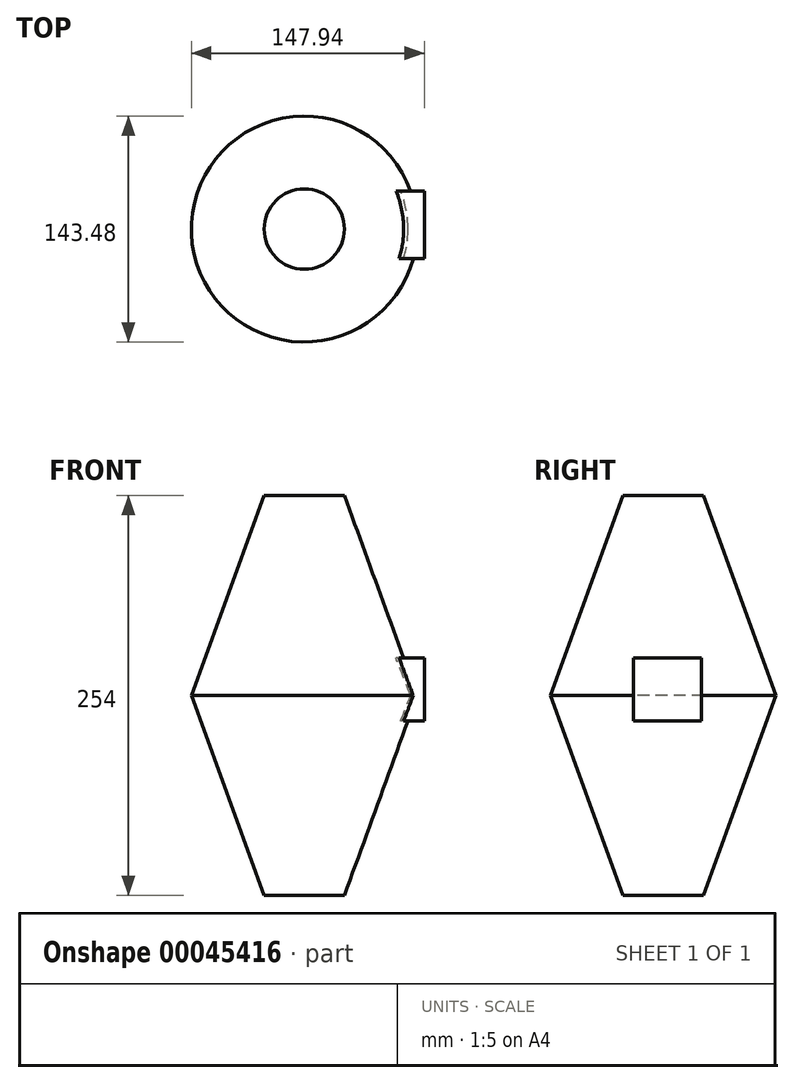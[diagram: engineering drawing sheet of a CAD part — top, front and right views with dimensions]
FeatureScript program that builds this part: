
annotation { "Feature Type Name" : "Feature", "Feature Type Description" : "" }
export const myFeature = defineFeature(function(context is Context, id is Id, definition is map)
    precondition{}
    {
        {
            var Q0;
            Q0=qCreatedBy(makeId("Top.planeOp"),FACE);
            var sketch = newSketch(context, id + "F0", { "sketchPlane" : qUnion([Q0])});
            skCircle(sketch, "E0", {"center": v(0, 0) * mm, "radius": 71.74 * mm});
            skSolve(sketch);
        }
        {
            var Q0;
            Q0 = qSketchRegion(id + "F0", true);
            extrude(context, id + "F1", {"entities" : qUnion([Q0]), "endBound" : BoundingType.SYMMETRIC, "depth" : 254 * mm, "hasDraft" : true, "draftAngle" : 20 * degree, "draftPullDirection" : true});
        }
        {
            var Q0;
            Q0=qCreatedBy(makeId("Right.planeOp"),FACE);
            var sketch = newSketch(context, id + "F2", { "sketchPlane" : qUnion([Q0])});
            skLineSegment(sketch, "E1.bottom", {"start": v(-18.76, -16.13) * mm, "end": v(24.17, -16.13) * mm});
            skLineSegment(sketch, "E1.top", {"start": v(-18.76, 23.72) * mm, "end": v(24.17, 23.72) * mm});
            skLineSegment(sketch, "E1.left", {"start": v(-18.76, -16.13) * mm, "end": v(-18.76, 23.72) * mm});
            skLineSegment(sketch, "E1.right", {"start": v(24.17, -16.13) * mm, "end": v(24.17, 23.72) * mm});
            skSolve(sketch);
        }
        {
            var Q0;
            Q0 = qSketchRegion(id + "F2", true);
            extrude(context, id + "F3", {"entities" : qUnion([Q0]), "operationType" : NewBodyOperationType.ADD, "depth" : 76.2 * mm});
        }
    });
